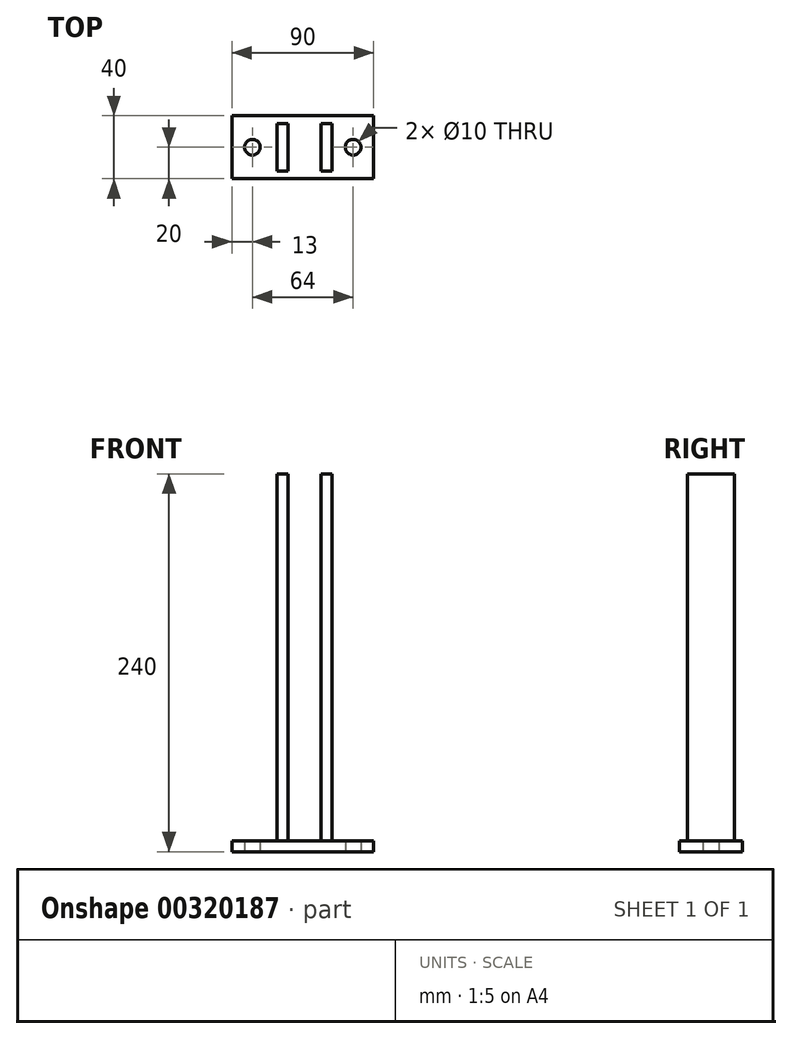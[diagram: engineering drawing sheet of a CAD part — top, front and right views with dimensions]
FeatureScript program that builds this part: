
annotation { "Feature Type Name" : "Feature", "Feature Type Description" : "" }
export const myFeature = defineFeature(function(context is Context, id is Id, definition is map)
    precondition{}
    {
        {
            var Q0;
            Q0=qCreatedBy(makeId("Right.planeOp"),FACE);
            var sketch = newSketch(context, id + "F0", { "sketchPlane" : qUnion([Q0])});
            skLineSegment(sketch, "E0.bottom", {"start": v(-20, 7) * mm, "end": v(20, 7) * mm});
            skLineSegment(sketch, "E0.left", {"start": v(-20, 7) * mm, "end": v(-20, 0) * mm});
            skLineSegment(sketch, "E0.right", {"start": v(20, 7) * mm, "end": v(20, 0) * mm});
            skLineSegment(sketch, "E1.trimOffspring", {"start": v(-20, 0) * mm, "end": v(20, 0) * mm});
            skSolve(sketch);
        }
        {
            var Q0;
            {var subQ3=sQuery(id+"F0.wireOp",EDGE,"ff7b447e-6627-4066-b775-27bb9192647b.left");Q0=makeQuery(id+"F0.imprint","IMPRINT",FACE,{"disambiguationData":[TD([[makeQuery(id+"F0.imprint","IMPRINT",EDGE,{"derivedFrom":subQ3}),-1.0]])]});}
            var Q1;
            {var subQ3=sQuery(id+"F0.wireOp",EDGE,"ff7b447e-6627-4066-b775-27bb9192647b.right");Q1=makeQuery(id+"F0.imprint","IMPRINT",FACE,{"disambiguationData":[TD([[makeQuery(id+"F0.imprint","IMPRINT",EDGE,{"derivedFrom":subQ3}),1.0]])]});}
            var Q2;
            {var subQ0=sQuery(id+"F0.wireOp",EDGE,"ff7b447e-6627-4066-b775-27bb9192647b.top");Q2=makeQuery(id+"F0.imprint","IMPRINT",FACE,{"disambiguationData":[TD([[makeQuery(id+"F0.imprint","IMPRINT",EDGE,{"derivedFrom":subQ0}),-1.0]])]});}
            var Q3;
            {var subQ5=sQuery(id+"F0.wireOp",EDGE,"E0.left");Q3=makeQuery(id+"F0.imprint","IMPRINT",FACE,{"disambiguationData":[TD([[makeQuery(id+"F0.imprint","IMPRINT",EDGE,{"derivedFrom":subQ5}),1.0]])]});}
            var Q4;
            {var subQ5=sQuery(id+"F0.wireOp",EDGE,"E0.right");Q4=makeQuery(id+"F0.imprint","IMPRINT",FACE,{"disambiguationData":[TD([[makeQuery(id+"F0.imprint","IMPRINT",EDGE,{"derivedFrom":subQ5}),-1.0]])]});}
            extrude(context, id + "F1", {"entities" : qUnion([Q0, Q1, Q2, Q3, Q4]), "depth" : 90 * mm});
        }
        {
            var Q0;
            Q0=qCreatedBy(makeId("Top.planeOp"),FACE);
            var sketch = newSketch(context, id + "F2", { "sketchPlane" : qUnion([Q0])});
            skLineSegment(sketch, "E2.bottom", {"start": v(27.5, 15) * mm, "end": v(34.5, 15) * mm});
            skLineSegment(sketch, "E2.top", {"start": v(27.5, -15) * mm, "end": v(34.5, -15) * mm});
            skLineSegment(sketch, "E2.left", {"start": v(27.5, 15) * mm, "end": v(27.5, -15) * mm});
            skLineSegment(sketch, "E2.right", {"start": v(34.5, 15) * mm, "end": v(34.5, -15) * mm});
            skLineSegment(sketch, "E3.bottom", {"start": v(55.5, 15) * mm, "end": v(62.5, 15) * mm});
            skLineSegment(sketch, "E3.top", {"start": v(55.5, -15) * mm, "end": v(62.5, -15) * mm});
            skLineSegment(sketch, "E3.left", {"start": v(55.5, 15) * mm, "end": v(55.5, -15) * mm});
            skLineSegment(sketch, "E3.right", {"start": v(62.5, 15) * mm, "end": v(62.5, -15) * mm});
            skLineSegment(sketch, "E4", {"start": v(0, -20) * mm, "end": v(90, -20) * mm, "construction": true});
            skLineSegment(sketch, "E5", {"start": v(90, 20) * mm, "end": v(90, -20) * mm, "construction": true});
            skPoint(sketch, "E6.center.orphan", {"position": v(77, 0) * mm});
            skPoint(sketch, "E7.center.orphan", {"position": v(13, 0) * mm});
            skSolve(sketch);
        }
        {
            var Q0;
            Q0=qCreatedBy(makeId("Top.planeOp"),FACE);
            var sketch = newSketch(context, id + "F3", { "sketchPlane" : qUnion([Q0])});
            skCircle(sketch, "E8", {"center": v(77, 0) * mm, "radius": 5 * mm});
            skCircle(sketch, "E9", {"center": v(13, 0) * mm, "radius": 5 * mm});
            skSolve(sketch);
        }
        {
            var Q0;
            Q0=sQuery(id+"F3.wireOp",VERTEX,"E9.center");
            var Q1;
            Q1=sQuery(id+"F3.wireOp",VERTEX,"E8.center");
            var Q2;
            Q2=makeQuery(id+"F1.opExtrude","SWEPT_BODY",BODY,{"disambiguationData":[OSD([sQuery(id+"F0.wireOp",EDGE,"E0.bottom"),sQuery(id+"F0.wireOp",EDGE,"E0.left"),sQuery(id+"F0.wireOp",EDGE,"E0.right"),sQuery(id+"F0.wireOp",EDGE,"E1.trimOffspring")])]});
            hole(context, id + "F4", {"style" : HoleStyle.SIMPLE, "endStyle" : HoleEndStyle.THROUGH, "oppositeDirection" : true, "holeDiameter" : 10 * mm, "tappedDepth" : 12 * mm, "tapClearance" : 3, "locations" : qUnion([Q0, Q1]), "scope" : qUnion([Q2])});
        }
        {
            var Q0;
            Q0=qCreatedBy(makeId("Front.planeOp"),FACE);
            var sketch = newSketch(context, id + "F5", { "sketchPlane" : qUnion([Q0])});
            skLineSegment(sketch, "E10.bottom", {"start": v(28.5, 240) * mm, "end": v(35.5, 240) * mm});
            skLineSegment(sketch, "E10.top", {"start": v(28.5, 0) * mm, "end": v(35.5, 0) * mm});
            skLineSegment(sketch, "E10.left", {"start": v(28.5, 240) * mm, "end": v(28.5, 0) * mm});
            skLineSegment(sketch, "E10.right", {"start": v(35.5, 240) * mm, "end": v(35.5, 0) * mm});
            skLineSegment(sketch, "E11.bottom", {"start": v(56.5, 240) * mm, "end": v(63.5, 240) * mm});
            skLineSegment(sketch, "E11.top", {"start": v(56.5, 0) * mm, "end": v(63.5, 0) * mm});
            skLineSegment(sketch, "E11.left", {"start": v(56.5, 240) * mm, "end": v(56.5, 0) * mm});
            skLineSegment(sketch, "E11.right", {"start": v(63.5, 240) * mm, "end": v(63.5, 0) * mm});
            skPoint(sketch, "E12.top.end.orphan", {"position": v(27.5, 245) * mm});
            skPoint(sketch, "E12.left.end.orphan", {"position": v(33.5, 245) * mm});
            skPoint(sketch, "E12.bottom.end.orphan", {"position": v(27.5, 215) * mm});
            skPoint(sketch, "E13.left.end.orphan", {"position": v(56.5, 245) * mm});
            skPoint(sketch, "E14.start.orphan", {"position": v(62.5, 215) * mm});
            skPoint(sketch, "E13.top.end.orphan", {"position": v(62.5, 245) * mm});
            skSolve(sketch);
        }
        {
            var Q0;
            Q0=makeQuery(id+"F5.imprint","IMPRINT",FACE,{"disambiguationData":[TD([[makeQuery(id+"F5.imprint","IMPRINT",EDGE,{"derivedFrom":sQuery(id+"F5.wireOp",EDGE,"E13.bottom")}),1.0]])]});
            var Q1;
            Q1=makeQuery(id+"F5.imprint","IMPRINT",FACE,{"disambiguationData":[TD([[makeQuery(id+"F5.imprint","IMPRINT",EDGE,{"derivedFrom":sQuery(id+"F5.wireOp",EDGE,"E11.bottom")}),1.0]])]});
            var Q2;
            Q2=makeQuery(id+"F5.imprint","IMPRINT",FACE,{"disambiguationData":[TD([[makeQuery(id+"F5.imprint","IMPRINT",EDGE,{"derivedFrom":sQuery(id+"F5.wireOp",EDGE,"E11.bottom")}),-1.0]])]});
            var Q3;
            Q3=makeQuery(id+"F5.imprint","IMPRINT",FACE,{"disambiguationData":[TD([[makeQuery(id+"F5.imprint","IMPRINT",EDGE,{"derivedFrom":sQuery(id+"F5.wireOp",EDGE,"E10.bottom")}),-1.0]])]});
            var Q4;
            Q4=makeQuery(id+"F5.imprint","IMPRINT",FACE,{"disambiguationData":[TD([[makeQuery(id+"F5.imprint","IMPRINT",EDGE,{"derivedFrom":sQuery(id+"F5.wireOp",EDGE,"E10.bottom")}),1.0]])]});
            var Q5;
            Q5=makeQuery(id+"F5.imprint","IMPRINT",FACE,{"disambiguationData":[TD([[makeQuery(id+"F5.imprint","IMPRINT",EDGE,{"derivedFrom":sQuery(id+"F5.wireOp",EDGE,"E12.bottom")}),-1.0]])]});
            extrude(context, id + "F6", {"entities" : qUnion([Q0, Q1, Q2, Q3, Q4, Q5]), "operationType" : NewBodyOperationType.ADD, "depth" : 15 * mm});
        }
        {
            var Q0;
            Q0=makeQuery(id+"F6.opExtrude","CAP_FACE",FACE,{"disambiguationData":[OSD([sQuery(id+"F5.wireOp",EDGE,"E10.top"),sQuery(id+"F5.wireOp",EDGE,"E10.left"),sQuery(id+"F5.wireOp",EDGE,"E10.right"),sQuery(id+"F5.wireOp",EDGE,"E12.top"),sQuery(id+"F5.wireOp",EDGE,"E12.left"),sQuery(id+"F5.wireOp",EDGE,"E12.right"),sQuery(id+"F5.wireOp",EDGE,"66f49a08-5c2f-4fd3-8abf-c2c6de82e6f8"),sQuery(id+"F5.wireOp",EDGE,"6f39bb26-9852-4725-b91f-57d0eff3294b")])],"isStart":true});
            var Q1;
            Q1=makeQuery(id+"F6.opExtrude","CAP_FACE",FACE,{"disambiguationData":[OSD([sQuery(id+"F5.wireOp",EDGE,"E11.top"),sQuery(id+"F5.wireOp",EDGE,"E11.left"),sQuery(id+"F5.wireOp",EDGE,"E11.right"),sQuery(id+"F5.wireOp",EDGE,"E13.top"),sQuery(id+"F5.wireOp",EDGE,"E13.left"),sQuery(id+"F5.wireOp",EDGE,"E13.right"),sQuery(id+"F5.wireOp",EDGE,"3ebc9420-5d92-4df4-82dc-56f84c2f9a30"),sQuery(id+"F5.wireOp",EDGE,"E14")])],"isStart":true});
            extrude(context, id + "F7", {"entities" : qUnion([Q0, Q1]), "operationType" : NewBodyOperationType.ADD, "depth" : 15 * mm});
        }
    });
